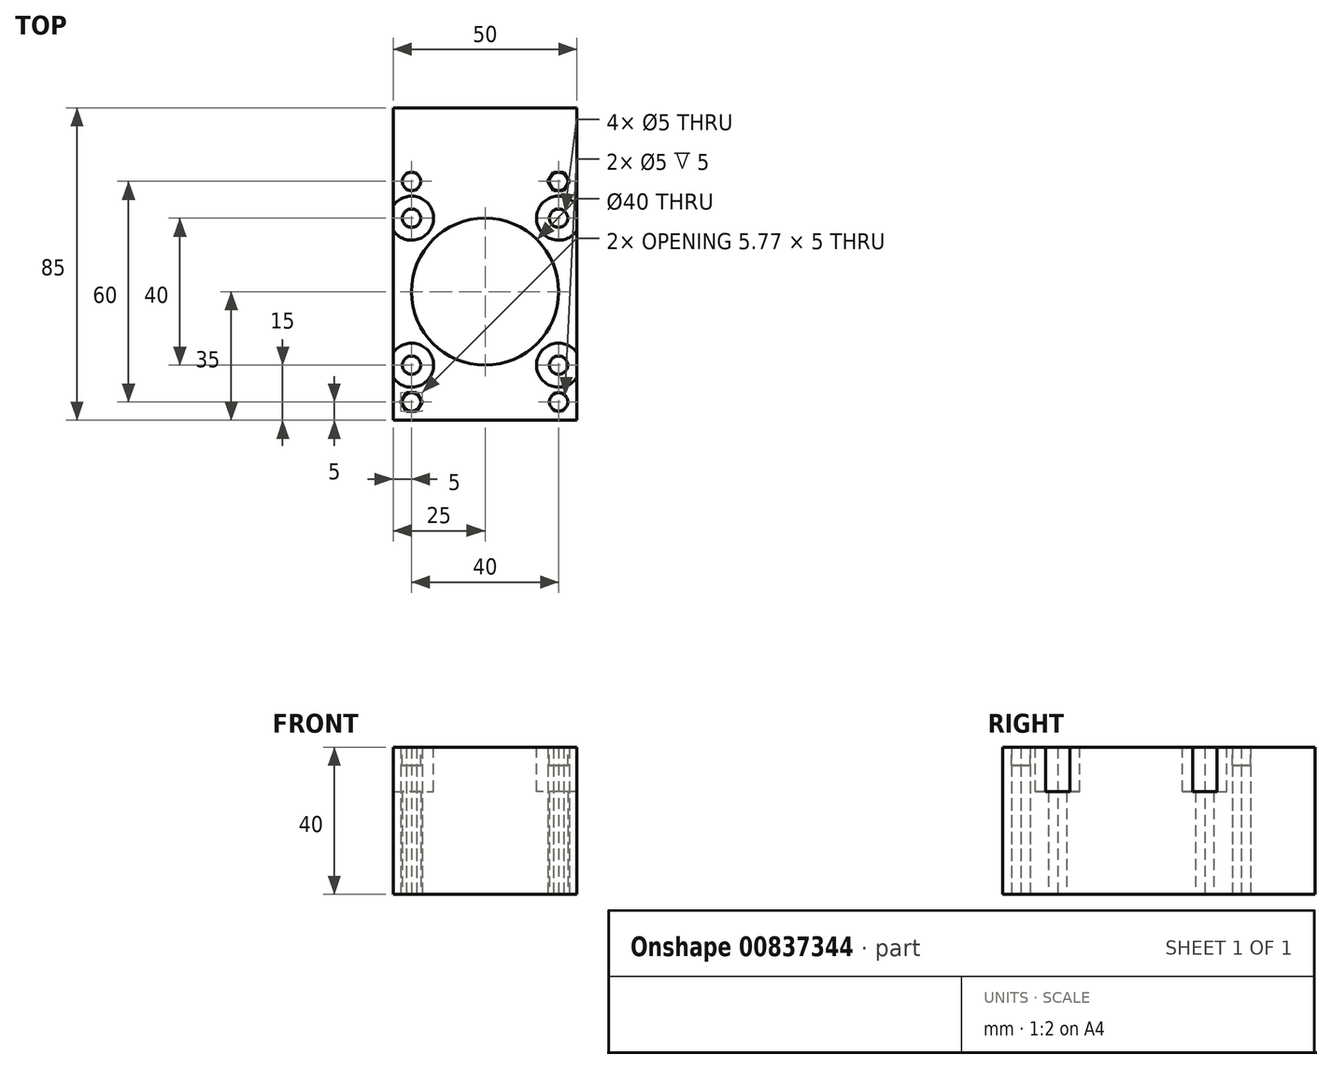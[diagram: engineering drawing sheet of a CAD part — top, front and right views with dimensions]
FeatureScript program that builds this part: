
annotation { "Feature Type Name" : "Feature", "Feature Type Description" : "" }
export const myFeature = defineFeature(function(context is Context, id is Id, definition is map)
    precondition{}
    {
        {
            var Q0;
            Q0=qCreatedBy(makeId("Top.planeOp"),FACE);
            var sketch = newSketch(context, id + "F0", { "sketchPlane" : qUnion([Q0])});
            skCircle(sketch, "E0", {"center": v(0, 0) * mm, "radius": 20 * mm});
            skLineSegment(sketch, "E1.bottom", {"start": v(-25, -35) * mm, "end": v(25, -35) * mm});
            skLineSegment(sketch, "E1.top", {"start": v(-25, 50) * mm, "end": v(25, 50) * mm});
            skLineSegment(sketch, "E1.left", {"start": v(-25, -35) * mm, "end": v(-25, 50) * mm});
            skLineSegment(sketch, "E1.right", {"start": v(25, -35) * mm, "end": v(25, 50) * mm});
            skCircle(sketch, "E2", {"center": v(20, 20) * mm, "radius": 2.5 * mm});
            skCircle(sketch, "E3.MirrorC", {"center": v(-20, 20) * mm, "radius": 2.5 * mm});
            skCircle(sketch, "E4.MirrorC", {"center": v(-20, -20) * mm, "radius": 2.5 * mm});
            skCircle(sketch, "E5.MirrorC", {"center": v(20, -20) * mm, "radius": 2.5 * mm});
            skCircle(sketch, "E6.cCircle", {"center": v(-20, -30) * mm, "radius": 2.5 * mm, "construction": true});
            skLineSegment(sketch, "E6.0", {"start": v(-18.56, -27.5) * mm, "end": v(-17.11, -30) * mm});
            skLineSegment(sketch, "E6.1", {"start": v(-17.11, -30) * mm, "end": v(-18.56, -32.5) * mm});
            skLineSegment(sketch, "E6.2", {"start": v(-18.56, -32.5) * mm, "end": v(-21.44, -32.5) * mm});
            skLineSegment(sketch, "E6.3", {"start": v(-21.44, -32.5) * mm, "end": v(-22.89, -30) * mm});
            skLineSegment(sketch, "E6.4", {"start": v(-22.89, -30) * mm, "end": v(-21.44, -27.5) * mm});
            skLineSegment(sketch, "E6.5", {"start": v(-21.44, -27.5) * mm, "end": v(-18.56, -27.5) * mm});
            skPoint(sketch, "E6.0.midPoint", {"position": v(-17.83, -28.75) * mm});
            skCircle(sketch, "E7.MirrorC", {"center": v(20, -30) * mm, "radius": 2.5 * mm, "construction": true});
            skLineSegment(sketch, "E8.MirrorCS", {"start": v(17.11, -30) * mm, "end": v(18.56, -32.5) * mm});
            skLineSegment(sketch, "E9.MirrorCS", {"start": v(18.56, -32.5) * mm, "end": v(21.44, -32.5) * mm});
            skLineSegment(sketch, "E10.MirrorCS", {"start": v(21.44, -32.5) * mm, "end": v(22.89, -30) * mm});
            skLineSegment(sketch, "E11.MirrorCS", {"start": v(22.89, -30) * mm, "end": v(21.44, -27.5) * mm});
            skLineSegment(sketch, "E12.MirrorCS", {"start": v(21.44, -27.5) * mm, "end": v(18.56, -27.5) * mm});
            skLineSegment(sketch, "E13.MirrorCS", {"start": v(18.56, -27.5) * mm, "end": v(17.11, -30) * mm});
            skLineSegment(sketch, "E14.MirrorCS", {"start": v(-21.44, 27.5) * mm, "end": v(-18.56, 27.5) * mm});
            skCircle(sketch, "E15.MirrorC", {"center": v(-20, 30) * mm, "radius": 2.5 * mm, "construction": true});
            skLineSegment(sketch, "E16.MirrorCS", {"start": v(-18.56, 27.5) * mm, "end": v(-17.11, 30) * mm});
            skLineSegment(sketch, "E17.MirrorCS", {"start": v(-17.11, 30) * mm, "end": v(-18.56, 32.5) * mm});
            skLineSegment(sketch, "E18.MirrorCS", {"start": v(-18.56, 32.5) * mm, "end": v(-21.44, 32.5) * mm});
            skLineSegment(sketch, "E19.MirrorCS", {"start": v(-21.44, 32.5) * mm, "end": v(-22.89, 30) * mm});
            skLineSegment(sketch, "E20.MirrorCS", {"start": v(-22.89, 30) * mm, "end": v(-21.44, 27.5) * mm});
            skCircle(sketch, "E21.MirrorC", {"center": v(20, 30) * mm, "radius": 2.5 * mm, "construction": true});
            skLineSegment(sketch, "E22.MirrorCS", {"start": v(18.56, 27.5) * mm, "end": v(17.11, 30) * mm});
            skLineSegment(sketch, "E23.MirrorCS", {"start": v(17.11, 30) * mm, "end": v(18.56, 32.5) * mm});
            skLineSegment(sketch, "E24.MirrorCS", {"start": v(21.44, 27.5) * mm, "end": v(18.56, 27.5) * mm});
            skLineSegment(sketch, "E25.MirrorCS", {"start": v(22.89, 30) * mm, "end": v(21.44, 27.5) * mm});
            skLineSegment(sketch, "E26.MirrorCS", {"start": v(21.44, 32.5) * mm, "end": v(22.89, 30) * mm});
            skLineSegment(sketch, "E27.MirrorCS", {"start": v(18.56, 32.5) * mm, "end": v(21.44, 32.5) * mm});
            skSolve(sketch);
        }
        {
            var Q0;
            Q0=makeQuery(id+"F0.imprint","IMPRINT",FACE,{"disambiguationData":[TD([[makeQuery(id+"F0.imprint","IMPRINT",EDGE,{"derivedFrom":sQuery(id+"F0.wireOp",EDGE,"E0")}),-1.0]])]});
            extrude(context, id + "F1", {"entities" : qUnion([Q0]), "depth" : 40 * mm, "offsetDistance" : 25 * mm});
        }
        {
            var Q0;
            Q0=makeQuery(id+"F1.opExtrude","CAP_FACE",FACE,{"disambiguationData":[OSD([sQuery(id+"F0.wireOp",EDGE,"E0"),sQuery(id+"F0.wireOp",EDGE,"E1.bottom"),sQuery(id+"F0.wireOp",EDGE,"E1.top"),sQuery(id+"F0.wireOp",EDGE,"E1.left"),sQuery(id+"F0.wireOp",EDGE,"E1.right"),sQuery(id+"F0.wireOp",EDGE,"E2"),sQuery(id+"F0.wireOp",EDGE,"E3.MirrorC"),sQuery(id+"F0.wireOp",EDGE,"E4.MirrorC"),sQuery(id+"F0.wireOp",EDGE,"E5.MirrorC"),sQuery(id+"F0.wireOp",EDGE,"E6.0"),sQuery(id+"F0.wireOp",EDGE,"E6.1"),sQuery(id+"F0.wireOp",EDGE,"E6.2"),sQuery(id+"F0.wireOp",EDGE,"E6.3"),sQuery(id+"F0.wireOp",EDGE,"E6.4"),sQuery(id+"F0.wireOp",EDGE,"E6.5"),sQuery(id+"F0.wireOp",EDGE,"E8.MirrorCS"),sQuery(id+"F0.wireOp",EDGE,"E9.MirrorCS"),sQuery(id+"F0.wireOp",EDGE,"E10.MirrorCS"),sQuery(id+"F0.wireOp",EDGE,"E11.MirrorCS"),sQuery(id+"F0.wireOp",EDGE,"E12.MirrorCS"),sQuery(id+"F0.wireOp",EDGE,"E13.MirrorCS"),sQuery(id+"F0.wireOp",EDGE,"E14.MirrorCS"),sQuery(id+"F0.wireOp",EDGE,"E16.MirrorCS"),sQuery(id+"F0.wireOp",EDGE,"E17.MirrorCS"),sQuery(id+"F0.wireOp",EDGE,"E18.MirrorCS"),sQuery(id+"F0.wireOp",EDGE,"E19.MirrorCS"),sQuery(id+"F0.wireOp",EDGE,"E20.MirrorCS"),sQuery(id+"F0.wireOp",EDGE,"E22.MirrorCS"),sQuery(id+"F0.wireOp",EDGE,"E23.MirrorCS"),sQuery(id+"F0.wireOp",EDGE,"E24.MirrorCS"),sQuery(id+"F0.wireOp",EDGE,"E25.MirrorCS"),sQuery(id+"F0.wireOp",EDGE,"E26.MirrorCS"),sQuery(id+"F0.wireOp",EDGE,"E27.MirrorCS")])],"isStart":false});
            var sketch = newSketch(context, id + "F2", { "sketchPlane" : qUnion([Q0])});
            skCircle(sketch, "E28", {"center": v(-20, 30) * mm, "radius": 2.5 * mm});
            skPoint(sketch, "E28.centerSnap0", {"position": v(-20, 32.5) * mm});
            skCircle(sketch, "E29.MirrorC", {"center": v(20, 30) * mm, "radius": 2.5 * mm});
            skCircle(sketch, "E30.MirrorC", {"center": v(20, -30) * mm, "radius": 2.5 * mm});
            skCircle(sketch, "E31.MirrorC", {"center": v(-20, -30) * mm, "radius": 2.5 * mm});
            skLineSegment(sketch, "E32.0", {"start": v(-18.56, 32.5) * mm, "end": v(-21.44, 32.5) * mm});
            skLineSegment(sketch, "E33.0", {"start": v(-21.44, 32.5) * mm, "end": v(-22.89, 30) * mm});
            skLineSegment(sketch, "E34.0", {"start": v(-22.89, 30) * mm, "end": v(-21.44, 27.5) * mm});
            skLineSegment(sketch, "E35.0", {"start": v(-21.44, 27.5) * mm, "end": v(-18.56, 27.5) * mm});
            skLineSegment(sketch, "E36.0", {"start": v(-18.56, 27.5) * mm, "end": v(-17.11, 30) * mm});
            skLineSegment(sketch, "E37.0", {"start": v(-17.11, 30) * mm, "end": v(-18.56, 32.5) * mm});
            skLineSegment(sketch, "E38.MirrorCS", {"start": v(17.11, 30) * mm, "end": v(18.56, 32.5) * mm});
            skLineSegment(sketch, "E39.MirrorCS", {"start": v(18.56, 32.5) * mm, "end": v(21.44, 32.5) * mm});
            skLineSegment(sketch, "E40.MirrorCS", {"start": v(21.44, 32.5) * mm, "end": v(22.89, 30) * mm});
            skLineSegment(sketch, "E41.MirrorCS", {"start": v(22.89, 30) * mm, "end": v(21.44, 27.5) * mm});
            skLineSegment(sketch, "E42.MirrorCS", {"start": v(21.44, 27.5) * mm, "end": v(18.56, 27.5) * mm});
            skLineSegment(sketch, "E43.MirrorCS", {"start": v(18.56, 27.5) * mm, "end": v(17.11, 30) * mm});
            skLineSegment(sketch, "E44.MirrorCS", {"start": v(-21.44, -27.5) * mm, "end": v(-18.56, -27.5) * mm});
            skLineSegment(sketch, "E45.MirrorCS", {"start": v(-22.89, -30) * mm, "end": v(-21.44, -27.5) * mm});
            skLineSegment(sketch, "E46.MirrorCS", {"start": v(-21.44, -32.5) * mm, "end": v(-22.89, -30) * mm});
            skLineSegment(sketch, "E47.MirrorCS", {"start": v(-18.56, -32.5) * mm, "end": v(-21.44, -32.5) * mm});
            skLineSegment(sketch, "E48.MirrorCS", {"start": v(-17.11, -30) * mm, "end": v(-18.56, -32.5) * mm});
            skLineSegment(sketch, "E49.MirrorCS", {"start": v(-18.56, -27.5) * mm, "end": v(-17.11, -30) * mm});
            skLineSegment(sketch, "E50.MirrorCS", {"start": v(18.56, -27.5) * mm, "end": v(17.11, -30) * mm});
            skLineSegment(sketch, "E51.MirrorCS", {"start": v(17.11, -30) * mm, "end": v(18.56, -32.5) * mm});
            skLineSegment(sketch, "E52.MirrorCS", {"start": v(18.56, -32.5) * mm, "end": v(21.44, -32.5) * mm});
            skLineSegment(sketch, "E53.MirrorCS", {"start": v(21.44, -32.5) * mm, "end": v(22.89, -30) * mm});
            skLineSegment(sketch, "E54.MirrorCS", {"start": v(22.89, -30) * mm, "end": v(21.44, -27.5) * mm});
            skLineSegment(sketch, "E55.MirrorCS", {"start": v(21.44, -27.5) * mm, "end": v(18.56, -27.5) * mm});
            skSolve(sketch);
        }
        {
            var Q0;
            {var subQ0=sQuery(id+"F2.wireOp",EDGE,"E32.0");var subQ1=sQuery(id+"F2.wireOp",EDGE,"E28");var subQ2=makeQuery(id+"F2.imprint","INTERSECT",VERTEX,{"derivedFrom":[subQ1,subQ0]});Q0=makeQuery(id+"F2.imprint","IMPRINT",FACE,{"disambiguationData":[TD([[makeQuery(id+"F2.imprint","IMPRINT",EDGE,{"disambiguationData":[TD([[subQ2,1.0]])],"derivedFrom":subQ1}),-1.0]])]});}
            var Q1;
            {var subQ0=sQuery(id+"F2.wireOp",EDGE,"E32.0");var subQ1=sQuery(id+"F2.wireOp",EDGE,"E28");var subQ2=makeQuery(id+"F2.imprint","INTERSECT",VERTEX,{"derivedFrom":[subQ1,subQ0]});Q1=makeQuery(id+"F2.imprint","IMPRINT",FACE,{"disambiguationData":[TD([[makeQuery(id+"F2.imprint","IMPRINT",EDGE,{"disambiguationData":[TD([[subQ2,-1.0]])],"derivedFrom":subQ1}),-1.0]])]});}
            var Q2;
            {var subQ0=sQuery(id+"F2.wireOp",EDGE,"E33.0");var subQ1=sQuery(id+"F2.wireOp",EDGE,"E28");var subQ2=makeQuery(id+"F2.imprint","INTERSECT",VERTEX,{"derivedFrom":[subQ1,subQ0]});Q2=makeQuery(id+"F2.imprint","IMPRINT",FACE,{"disambiguationData":[TD([[makeQuery(id+"F2.imprint","IMPRINT",EDGE,{"disambiguationData":[TD([[subQ2,-1.0]])],"derivedFrom":subQ1}),-1.0]])]});}
            var Q3;
            {var subQ0=sQuery(id+"F2.wireOp",EDGE,"E34.0");var subQ1=sQuery(id+"F2.wireOp",EDGE,"E28");var subQ2=makeQuery(id+"F2.imprint","INTERSECT",VERTEX,{"derivedFrom":[subQ1,subQ0]});Q3=makeQuery(id+"F2.imprint","IMPRINT",FACE,{"disambiguationData":[TD([[makeQuery(id+"F2.imprint","IMPRINT",EDGE,{"disambiguationData":[TD([[subQ2,-1.0]])],"derivedFrom":subQ1}),-1.0]])]});}
            var Q4;
            {var subQ0=sQuery(id+"F2.wireOp",EDGE,"E35.0");var subQ1=sQuery(id+"F2.wireOp",EDGE,"E28");var subQ2=makeQuery(id+"F2.imprint","INTERSECT",VERTEX,{"derivedFrom":[subQ1,subQ0]});Q4=makeQuery(id+"F2.imprint","IMPRINT",FACE,{"disambiguationData":[TD([[makeQuery(id+"F2.imprint","IMPRINT",EDGE,{"disambiguationData":[TD([[subQ2,-1.0]])],"derivedFrom":subQ1}),-1.0]])]});}
            var Q5;
            {var subQ0=sQuery(id+"F2.wireOp",EDGE,"E37.0");var subQ1=sQuery(id+"F2.wireOp",EDGE,"E28");var subQ2=makeQuery(id+"F2.imprint","INTERSECT",VERTEX,{"derivedFrom":[subQ1,subQ0]});Q5=makeQuery(id+"F2.imprint","IMPRINT",FACE,{"disambiguationData":[TD([[makeQuery(id+"F2.imprint","IMPRINT",EDGE,{"disambiguationData":[TD([[subQ2,1.0]])],"derivedFrom":subQ1}),-1.0]])]});}
            var Q6;
            {var subQ0=sQuery(id+"F2.wireOp",EDGE,"E39.MirrorCS");var subQ1=sQuery(id+"F2.wireOp",EDGE,"E29.MirrorC");var subQ2=makeQuery(id+"F2.imprint","INTERSECT",VERTEX,{"derivedFrom":[subQ1,subQ0]});Q6=makeQuery(id+"F2.imprint","IMPRINT",FACE,{"disambiguationData":[TD([[makeQuery(id+"F2.imprint","IMPRINT",EDGE,{"disambiguationData":[TD([[subQ2,1.0]])],"derivedFrom":subQ1}),1.0]])]});}
            var Q7;
            {var subQ0=sQuery(id+"F2.wireOp",EDGE,"E39.MirrorCS");var subQ1=sQuery(id+"F2.wireOp",EDGE,"E29.MirrorC");var subQ2=makeQuery(id+"F2.imprint","INTERSECT",VERTEX,{"derivedFrom":[subQ1,subQ0]});Q7=makeQuery(id+"F2.imprint","IMPRINT",FACE,{"disambiguationData":[TD([[makeQuery(id+"F2.imprint","IMPRINT",EDGE,{"disambiguationData":[TD([[subQ2,-1.0]])],"derivedFrom":subQ1}),1.0]])]});}
            var Q8;
            {var subQ0=sQuery(id+"F2.wireOp",EDGE,"E40.MirrorCS");var subQ1=sQuery(id+"F2.wireOp",EDGE,"E29.MirrorC");var subQ2=makeQuery(id+"F2.imprint","INTERSECT",VERTEX,{"derivedFrom":[subQ1,subQ0]});Q8=makeQuery(id+"F2.imprint","IMPRINT",FACE,{"disambiguationData":[TD([[makeQuery(id+"F2.imprint","IMPRINT",EDGE,{"disambiguationData":[TD([[subQ2,-1.0]])],"derivedFrom":subQ1}),1.0]])]});}
            var Q9;
            {var subQ0=sQuery(id+"F2.wireOp",EDGE,"E41.MirrorCS");var subQ1=sQuery(id+"F2.wireOp",EDGE,"E29.MirrorC");var subQ2=makeQuery(id+"F2.imprint","INTERSECT",VERTEX,{"derivedFrom":[subQ1,subQ0]});Q9=makeQuery(id+"F2.imprint","IMPRINT",FACE,{"disambiguationData":[TD([[makeQuery(id+"F2.imprint","IMPRINT",EDGE,{"disambiguationData":[TD([[subQ2,-1.0]])],"derivedFrom":subQ1}),1.0]])]});}
            var Q10;
            {var subQ0=sQuery(id+"F2.wireOp",EDGE,"E42.MirrorCS");var subQ1=sQuery(id+"F2.wireOp",EDGE,"E29.MirrorC");var subQ2=makeQuery(id+"F2.imprint","INTERSECT",VERTEX,{"derivedFrom":[subQ1,subQ0]});Q10=makeQuery(id+"F2.imprint","IMPRINT",FACE,{"disambiguationData":[TD([[makeQuery(id+"F2.imprint","IMPRINT",EDGE,{"disambiguationData":[TD([[subQ2,-1.0]])],"derivedFrom":subQ1}),1.0]])]});}
            var Q11;
            {var subQ0=sQuery(id+"F2.wireOp",EDGE,"E38.MirrorCS");var subQ1=sQuery(id+"F2.wireOp",EDGE,"E29.MirrorC");var subQ2=makeQuery(id+"F2.imprint","INTERSECT",VERTEX,{"derivedFrom":[subQ1,subQ0]});Q11=makeQuery(id+"F2.imprint","IMPRINT",FACE,{"disambiguationData":[TD([[makeQuery(id+"F2.imprint","IMPRINT",EDGE,{"disambiguationData":[TD([[subQ2,1.0]])],"derivedFrom":subQ1}),1.0]])]});}
            var Q12;
            {var subQ0=sQuery(id+"F2.wireOp",EDGE,"E52.MirrorCS");var subQ1=sQuery(id+"F2.wireOp",EDGE,"E30.MirrorC");var subQ2=makeQuery(id+"F2.imprint","INTERSECT",VERTEX,{"derivedFrom":[subQ1,subQ0]});Q12=makeQuery(id+"F2.imprint","IMPRINT",FACE,{"disambiguationData":[TD([[makeQuery(id+"F2.imprint","IMPRINT",EDGE,{"disambiguationData":[TD([[subQ2,1.0]])],"derivedFrom":subQ1}),-1.0]])]});}
            var Q13;
            {var subQ0=sQuery(id+"F2.wireOp",EDGE,"E52.MirrorCS");var subQ1=sQuery(id+"F2.wireOp",EDGE,"E30.MirrorC");var subQ2=makeQuery(id+"F2.imprint","INTERSECT",VERTEX,{"derivedFrom":[subQ1,subQ0]});Q13=makeQuery(id+"F2.imprint","IMPRINT",FACE,{"disambiguationData":[TD([[makeQuery(id+"F2.imprint","IMPRINT",EDGE,{"disambiguationData":[TD([[subQ2,-1.0]])],"derivedFrom":subQ1}),-1.0]])]});}
            var Q14;
            {var subQ0=sQuery(id+"F2.wireOp",EDGE,"E53.MirrorCS");var subQ1=sQuery(id+"F2.wireOp",EDGE,"E30.MirrorC");var subQ2=makeQuery(id+"F2.imprint","INTERSECT",VERTEX,{"derivedFrom":[subQ1,subQ0]});Q14=makeQuery(id+"F2.imprint","IMPRINT",FACE,{"disambiguationData":[TD([[makeQuery(id+"F2.imprint","IMPRINT",EDGE,{"disambiguationData":[TD([[subQ2,-1.0]])],"derivedFrom":subQ1}),-1.0]])]});}
            var Q15;
            {var subQ0=sQuery(id+"F2.wireOp",EDGE,"E54.MirrorCS");var subQ1=sQuery(id+"F2.wireOp",EDGE,"E30.MirrorC");var subQ2=makeQuery(id+"F2.imprint","INTERSECT",VERTEX,{"derivedFrom":[subQ1,subQ0]});Q15=makeQuery(id+"F2.imprint","IMPRINT",FACE,{"disambiguationData":[TD([[makeQuery(id+"F2.imprint","IMPRINT",EDGE,{"disambiguationData":[TD([[subQ2,-1.0]])],"derivedFrom":subQ1}),-1.0]])]});}
            var Q16;
            {var subQ0=sQuery(id+"F2.wireOp",EDGE,"E55.MirrorCS");var subQ1=sQuery(id+"F2.wireOp",EDGE,"E30.MirrorC");var subQ2=makeQuery(id+"F2.imprint","INTERSECT",VERTEX,{"derivedFrom":[subQ1,subQ0]});Q16=makeQuery(id+"F2.imprint","IMPRINT",FACE,{"disambiguationData":[TD([[makeQuery(id+"F2.imprint","IMPRINT",EDGE,{"disambiguationData":[TD([[subQ2,-1.0]])],"derivedFrom":subQ1}),-1.0]])]});}
            var Q17;
            {var subQ0=sQuery(id+"F2.wireOp",EDGE,"E51.MirrorCS");var subQ1=sQuery(id+"F2.wireOp",EDGE,"E30.MirrorC");var subQ2=makeQuery(id+"F2.imprint","INTERSECT",VERTEX,{"derivedFrom":[subQ1,subQ0]});Q17=makeQuery(id+"F2.imprint","IMPRINT",FACE,{"disambiguationData":[TD([[makeQuery(id+"F2.imprint","IMPRINT",EDGE,{"disambiguationData":[TD([[subQ2,1.0]])],"derivedFrom":subQ1}),-1.0]])]});}
            var Q18;
            {var subQ0=sQuery(id+"F2.wireOp",EDGE,"E47.MirrorCS");var subQ1=sQuery(id+"F2.wireOp",EDGE,"E31.MirrorC");var subQ2=makeQuery(id+"F2.imprint","INTERSECT",VERTEX,{"derivedFrom":[subQ1,subQ0]});Q18=makeQuery(id+"F2.imprint","IMPRINT",FACE,{"disambiguationData":[TD([[makeQuery(id+"F2.imprint","IMPRINT",EDGE,{"disambiguationData":[TD([[subQ2,1.0]])],"derivedFrom":subQ1}),1.0]])]});}
            var Q19;
            {var subQ0=sQuery(id+"F2.wireOp",EDGE,"E47.MirrorCS");var subQ1=sQuery(id+"F2.wireOp",EDGE,"E31.MirrorC");var subQ2=makeQuery(id+"F2.imprint","INTERSECT",VERTEX,{"derivedFrom":[subQ1,subQ0]});Q19=makeQuery(id+"F2.imprint","IMPRINT",FACE,{"disambiguationData":[TD([[makeQuery(id+"F2.imprint","IMPRINT",EDGE,{"disambiguationData":[TD([[subQ2,-1.0]])],"derivedFrom":subQ1}),1.0]])]});}
            var Q20;
            {var subQ0=sQuery(id+"F2.wireOp",EDGE,"E46.MirrorCS");var subQ1=sQuery(id+"F2.wireOp",EDGE,"E31.MirrorC");var subQ2=makeQuery(id+"F2.imprint","INTERSECT",VERTEX,{"derivedFrom":[subQ1,subQ0]});Q20=makeQuery(id+"F2.imprint","IMPRINT",FACE,{"disambiguationData":[TD([[makeQuery(id+"F2.imprint","IMPRINT",EDGE,{"disambiguationData":[TD([[subQ2,-1.0]])],"derivedFrom":subQ1}),1.0]])]});}
            var Q21;
            {var subQ0=sQuery(id+"F2.wireOp",EDGE,"E45.MirrorCS");var subQ1=sQuery(id+"F2.wireOp",EDGE,"E31.MirrorC");var subQ2=makeQuery(id+"F2.imprint","INTERSECT",VERTEX,{"derivedFrom":[subQ1,subQ0]});Q21=makeQuery(id+"F2.imprint","IMPRINT",FACE,{"disambiguationData":[TD([[makeQuery(id+"F2.imprint","IMPRINT",EDGE,{"disambiguationData":[TD([[subQ2,-1.0]])],"derivedFrom":subQ1}),1.0]])]});}
            var Q22;
            {var subQ0=sQuery(id+"F2.wireOp",EDGE,"E44.MirrorCS");var subQ1=sQuery(id+"F2.wireOp",EDGE,"E31.MirrorC");var subQ2=makeQuery(id+"F2.imprint","INTERSECT",VERTEX,{"derivedFrom":[subQ1,subQ0]});Q22=makeQuery(id+"F2.imprint","IMPRINT",FACE,{"disambiguationData":[TD([[makeQuery(id+"F2.imprint","IMPRINT",EDGE,{"disambiguationData":[TD([[subQ2,-1.0]])],"derivedFrom":subQ1}),1.0]])]});}
            var Q23;
            {var subQ0=sQuery(id+"F2.wireOp",EDGE,"E48.MirrorCS");var subQ1=sQuery(id+"F2.wireOp",EDGE,"E31.MirrorC");var subQ2=makeQuery(id+"F2.imprint","INTERSECT",VERTEX,{"derivedFrom":[subQ1,subQ0]});Q23=makeQuery(id+"F2.imprint","IMPRINT",FACE,{"disambiguationData":[TD([[makeQuery(id+"F2.imprint","IMPRINT",EDGE,{"disambiguationData":[TD([[subQ2,1.0]])],"derivedFrom":subQ1}),1.0]])]});}
            extrude(context, id + "F3", {"entities" : qUnion([Q0, Q1, Q2, Q3, Q4, Q5, Q6, Q7, Q8, Q9, Q10, Q11, Q12, Q13, Q14, Q15, Q16, Q17, Q18, Q19, Q20, Q21, Q22, Q23]), "operationType" : NewBodyOperationType.ADD, "oppositeDirection" : true, "depth" : 5 * mm, "offsetDistance" : 25 * mm});
        }
        {
            var Q0;
            {var subQ0=sQuery(id+"F2.wireOp",EDGE,"E49.MirrorCS");var subQ1=sQuery(id+"F2.wireOp",EDGE,"E48.MirrorCS");var subQ2=sQuery(id+"F2.wireOp",EDGE,"E31.MirrorC");var subQ3=sQuery(id+"F2.wireOp",EDGE,"E44.MirrorCS");var subQ4=sQuery(id+"F2.wireOp",EDGE,"E45.MirrorCS");var subQ5=sQuery(id+"F2.wireOp",EDGE,"E46.MirrorCS");var subQ6=sQuery(id+"F2.wireOp",EDGE,"E47.MirrorCS");var subQ7=sQuery(id+"F2.wireOp",EDGE,"E51.MirrorCS");var subQ8=sQuery(id+"F2.wireOp",EDGE,"E50.MirrorCS");var subQ9=sQuery(id+"F2.wireOp",EDGE,"E30.MirrorC");var subQ10=sQuery(id+"F2.wireOp",EDGE,"E55.MirrorCS");var subQ11=sQuery(id+"F2.wireOp",EDGE,"E54.MirrorCS");var subQ12=sQuery(id+"F2.wireOp",EDGE,"E53.MirrorCS");var subQ13=sQuery(id+"F2.wireOp",EDGE,"E52.MirrorCS");var subQ14=sQuery(id+"F2.wireOp",EDGE,"E43.MirrorCS");var subQ15=sQuery(id+"F2.wireOp",EDGE,"E38.MirrorCS");var subQ16=sQuery(id+"F2.wireOp",EDGE,"E29.MirrorC");var subQ17=sQuery(id+"F2.wireOp",EDGE,"E42.MirrorCS");var subQ18=sQuery(id+"F2.wireOp",EDGE,"E41.MirrorCS");var subQ19=sQuery(id+"F2.wireOp",EDGE,"E40.MirrorCS");var subQ20=sQuery(id+"F2.wireOp",EDGE,"E39.MirrorCS");var subQ21=sQuery(id+"F2.wireOp",EDGE,"E37.0");var subQ22=sQuery(id+"F2.wireOp",EDGE,"E36.0");var subQ23=sQuery(id+"F2.wireOp",EDGE,"E28");var subQ24=sQuery(id+"F2.wireOp",EDGE,"E35.0");var subQ25=sQuery(id+"F2.wireOp",EDGE,"E34.0");var subQ26=sQuery(id+"F2.wireOp",EDGE,"E33.0");var subQ27=sQuery(id+"F2.wireOp",EDGE,"E32.0");Q0=makeQuery(id+"F3.boolean.opBoolean","MERGE",FACE,{"derivedFrom":[makeQuery(id+"F1.opExtrude","CAP_FACE",FACE,{"disambiguationData":[OSD([sQuery(id+"F0.wireOp",EDGE,"E0"),sQuery(id+"F0.wireOp",EDGE,"E1.bottom"),sQuery(id+"F0.wireOp",EDGE,"E1.top"),sQuery(id+"F0.wireOp",EDGE,"E1.left"),sQuery(id+"F0.wireOp",EDGE,"E1.right"),sQuery(id+"F0.wireOp",EDGE,"E2"),sQuery(id+"F0.wireOp",EDGE,"E3.MirrorC"),sQuery(id+"F0.wireOp",EDGE,"E4.MirrorC"),sQuery(id+"F0.wireOp",EDGE,"E5.MirrorC"),sQuery(id+"F0.wireOp",EDGE,"E6.0"),sQuery(id+"F0.wireOp",EDGE,"E6.1"),sQuery(id+"F0.wireOp",EDGE,"E6.2"),sQuery(id+"F0.wireOp",EDGE,"E6.3"),sQuery(id+"F0.wireOp",EDGE,"E6.4"),sQuery(id+"F0.wireOp",EDGE,"E6.5"),sQuery(id+"F0.wireOp",EDGE,"E8.MirrorCS"),sQuery(id+"F0.wireOp",EDGE,"E9.MirrorCS"),sQuery(id+"F0.wireOp",EDGE,"E10.MirrorCS"),sQuery(id+"F0.wireOp",EDGE,"E11.MirrorCS"),sQuery(id+"F0.wireOp",EDGE,"E12.MirrorCS"),sQuery(id+"F0.wireOp",EDGE,"E13.MirrorCS"),sQuery(id+"F0.wireOp",EDGE,"E14.MirrorCS"),sQuery(id+"F0.wireOp",EDGE,"E16.MirrorCS"),sQuery(id+"F0.wireOp",EDGE,"E17.MirrorCS"),sQuery(id+"F0.wireOp",EDGE,"E18.MirrorCS"),sQuery(id+"F0.wireOp",EDGE,"E19.MirrorCS"),sQuery(id+"F0.wireOp",EDGE,"E20.MirrorCS"),sQuery(id+"F0.wireOp",EDGE,"E22.MirrorCS"),sQuery(id+"F0.wireOp",EDGE,"E23.MirrorCS"),sQuery(id+"F0.wireOp",EDGE,"E24.MirrorCS"),sQuery(id+"F0.wireOp",EDGE,"E25.MirrorCS"),sQuery(id+"F0.wireOp",EDGE,"E26.MirrorCS"),sQuery(id+"F0.wireOp",EDGE,"E27.MirrorCS")])],"isStart":false}),makeQuery(id+"F3.opExtrude","CAP_FACE",FACE,{"disambiguationData":[OSD([subQ23,subQ27,subQ21])],"isStart":true}),makeQuery(id+"F3.opExtrude","CAP_FACE",FACE,{"disambiguationData":[OSD([subQ23,subQ27,subQ26])],"isStart":true}),makeQuery(id+"F3.opExtrude","CAP_FACE",FACE,{"disambiguationData":[OSD([subQ23,subQ26,subQ25])],"isStart":true}),makeQuery(id+"F3.opExtrude","CAP_FACE",FACE,{"disambiguationData":[OSD([subQ23,subQ25,subQ24])],"isStart":true}),makeQuery(id+"F3.opExtrude","CAP_FACE",FACE,{"disambiguationData":[OSD([subQ23,subQ24,subQ22])],"isStart":true}),makeQuery(id+"F3.opExtrude","CAP_FACE",FACE,{"disambiguationData":[OSD([subQ23,subQ22,subQ21])],"isStart":true}),makeQuery(id+"F3.opExtrude","CAP_FACE",FACE,{"disambiguationData":[OSD([subQ16,subQ15,subQ20])],"isStart":true}),makeQuery(id+"F3.opExtrude","CAP_FACE",FACE,{"disambiguationData":[OSD([subQ16,subQ20,subQ19])],"isStart":true}),makeQuery(id+"F3.opExtrude","CAP_FACE",FACE,{"disambiguationData":[OSD([subQ16,subQ19,subQ18])],"isStart":true}),makeQuery(id+"F3.opExtrude","CAP_FACE",FACE,{"disambiguationData":[OSD([subQ16,subQ18,subQ17])],"isStart":true}),makeQuery(id+"F3.opExtrude","CAP_FACE",FACE,{"disambiguationData":[OSD([subQ16,subQ17,subQ14])],"isStart":true}),makeQuery(id+"F3.opExtrude","CAP_FACE",FACE,{"disambiguationData":[OSD([subQ16,subQ15,subQ14])],"isStart":true}),makeQuery(id+"F3.opExtrude","CAP_FACE",FACE,{"disambiguationData":[OSD([subQ9,subQ7,subQ13])],"isStart":true}),makeQuery(id+"F3.opExtrude","CAP_FACE",FACE,{"disambiguationData":[OSD([subQ9,subQ13,subQ12])],"isStart":true}),makeQuery(id+"F3.opExtrude","CAP_FACE",FACE,{"disambiguationData":[OSD([subQ9,subQ12,subQ11])],"isStart":true}),makeQuery(id+"F3.opExtrude","CAP_FACE",FACE,{"disambiguationData":[OSD([subQ9,subQ11,subQ10])],"isStart":true}),makeQuery(id+"F3.opExtrude","CAP_FACE",FACE,{"disambiguationData":[OSD([subQ9,subQ8,subQ10])],"isStart":true}),makeQuery(id+"F3.opExtrude","CAP_FACE",FACE,{"disambiguationData":[OSD([subQ9,subQ8,subQ7])],"isStart":true}),makeQuery(id+"F3.opExtrude","CAP_FACE",FACE,{"disambiguationData":[OSD([subQ2,subQ6,subQ1])],"isStart":true}),makeQuery(id+"F3.opExtrude","CAP_FACE",FACE,{"disambiguationData":[OSD([subQ2,subQ5,subQ6])],"isStart":true}),makeQuery(id+"F3.opExtrude","CAP_FACE",FACE,{"disambiguationData":[OSD([subQ2,subQ4,subQ5])],"isStart":true}),makeQuery(id+"F3.opExtrude","CAP_FACE",FACE,{"disambiguationData":[OSD([subQ2,subQ3,subQ4])],"isStart":true}),makeQuery(id+"F3.opExtrude","CAP_FACE",FACE,{"disambiguationData":[OSD([subQ2,subQ3,subQ0])],"isStart":true}),makeQuery(id+"F3.opExtrude","CAP_FACE",FACE,{"disambiguationData":[OSD([subQ2,subQ1,subQ0])],"isStart":true})]});}
            var sketch = newSketch(context, id + "F4", { "sketchPlane" : qUnion([Q0])});
            skCircle(sketch, "E56", {"center": v(-20, -20) * mm, "radius": 6 * mm});
            skCircle(sketch, "E57.MirrorC", {"center": v(20, -20) * mm, "radius": 6 * mm});
            skCircle(sketch, "E58.MirrorC", {"center": v(-20, 20) * mm, "radius": 6 * mm});
            skCircle(sketch, "E59.MirrorC", {"center": v(20, 20) * mm, "radius": 6 * mm});
            skSolve(sketch);
        }
        {
            var Q0;
            Q0 = qSketchRegion(id + "F4", true);
            extrude(context, id + "F5", {"entities" : qUnion([Q0]), "operationType" : NewBodyOperationType.REMOVE, "oppositeDirection" : true, "depth" : 12 * mm, "offsetDistance" : 25 * mm});
        }
    });
